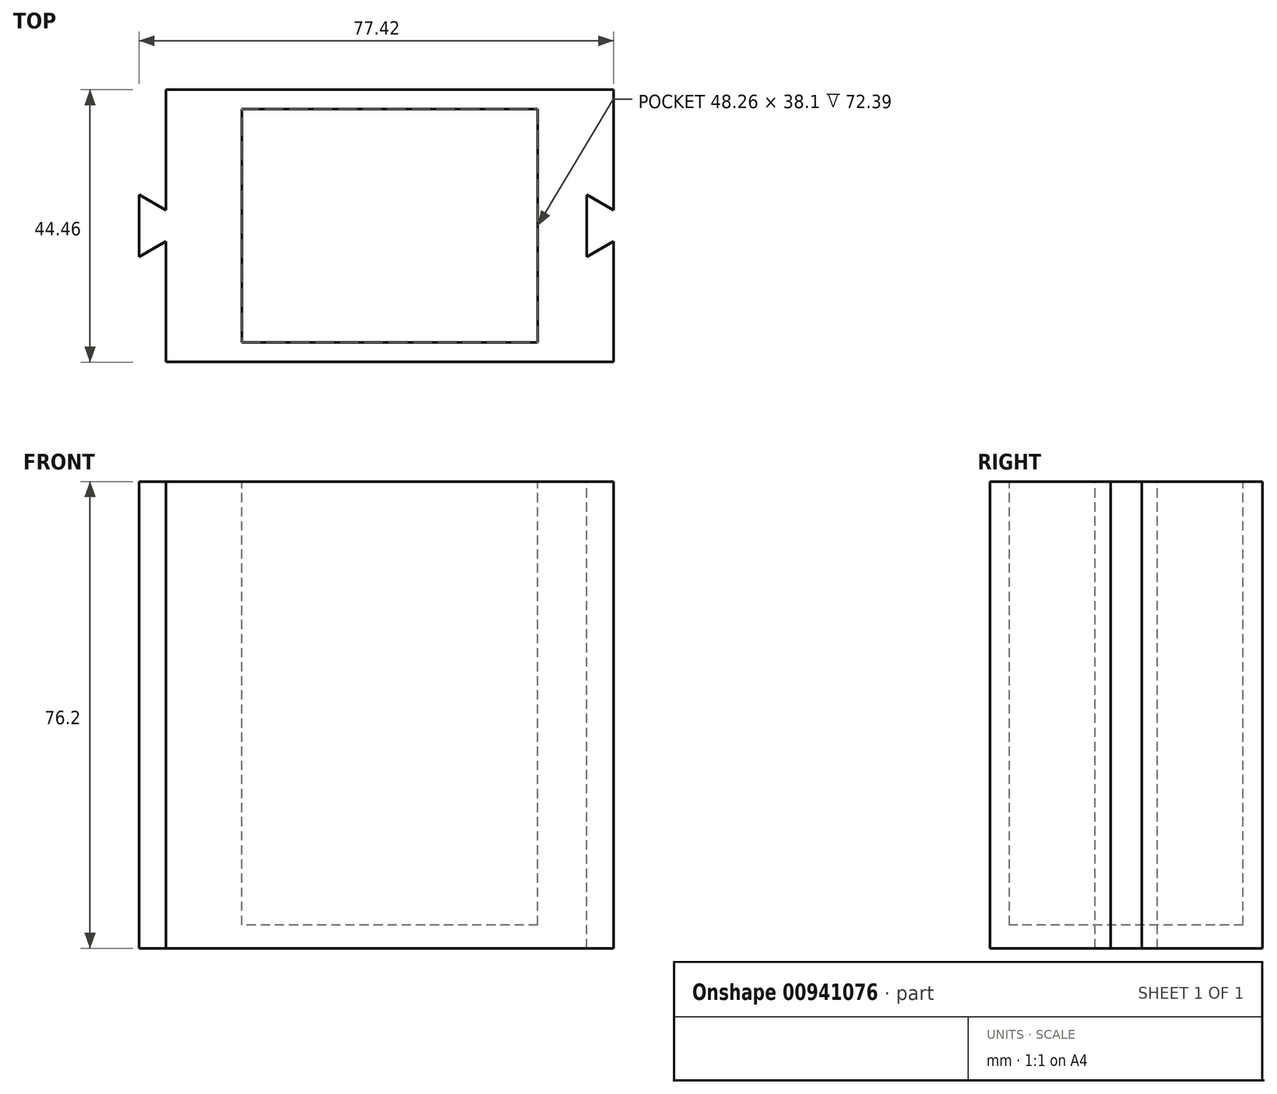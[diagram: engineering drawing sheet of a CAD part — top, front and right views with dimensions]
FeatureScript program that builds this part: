
annotation { "Feature Type Name" : "Feature", "Feature Type Description" : "" }
export const myFeature = defineFeature(function(context is Context, id is Id, definition is map)
    precondition{}
    {
        {
            var Q0;
            Q0=qCreatedBy(makeId("Top.planeOp"),FACE);
            var sketch = newSketch(context, id + "F0", { "sketchPlane" : qUnion([Q0])});
            skLineSegment(sketch, "E0.bottom", {"start": v(36.51, 22.23) * mm, "end": v(-36.51, 22.23) * mm});
            skLineSegment(sketch, "E0.top", {"start": v(36.51, -22.22) * mm, "end": v(-36.51, -22.22) * mm});
            skLineSegment(sketch, "E0.left", {"start": v(36.51, 22.23) * mm, "end": v(36.51, -22.22) * mm});
            skLineSegment(sketch, "E0.right", {"start": v(-36.51, 22.23) * mm, "end": v(-36.51, -22.22) * mm});
            skPoint(sketch, "E0.middle", {"position": v(0, 0) * mm});
            skSolve(sketch);
        }
        {
            var Q0;
            Q0=makeQuery(id+"F0.imprint","IMPRINT",FACE,{"disambiguationData":[TD([[makeQuery(id+"F0.imprint","IMPRINT",EDGE,{"derivedFrom":sQuery(id+"F0.wireOp",EDGE,"E0.bottom")}),1.0]])]});
            extrude(context, id + "F1", {"entities" : qUnion([Q0]), "depth" : 76.2 * mm, "offsetDistance" : 25.4 * mm});
        }
        {
            var Q0;
            Q0=makeQuery(id+"F1.opExtrude","CAP_FACE",FACE,{"disambiguationData":[OSD([sQuery(id+"F0.wireOp",EDGE,"E0.bottom"),sQuery(id+"F0.wireOp",EDGE,"E0.top"),sQuery(id+"F0.wireOp",EDGE,"E0.left"),sQuery(id+"F0.wireOp",EDGE,"E0.right")])],"isStart":false});
            var sketch = newSketch(context, id + "F2", { "sketchPlane" : qUnion([Q0])});
            skLineSegment(sketch, "E1.bottom", {"start": v(0, -22.22) * mm, "end": v(0, -22.22) * mm});
            skLineSegment(sketch, "E1.top", {"start": v(0, 66.68) * mm, "end": v(0, 66.68) * mm});
            skLineSegment(sketch, "E1.left", {"start": v(0, -22.22) * mm, "end": v(0, 66.68) * mm, "construction": true});
            skLineSegment(sketch, "E1.right", {"start": v(0, -22.22) * mm, "end": v(0, 66.68) * mm, "construction": true});
            skPoint(sketch, "E1.middle", {"position": v(0, 22.23) * mm});
            skLineSegment(sketch, "E2", {"start": v(-36.51, 0) * mm, "end": v(36.51, 0) * mm, "construction": true});
            skLineSegment(sketch, "E3.bottom", {"start": v(24.13, 19.05) * mm, "end": v(-24.13, 19.05) * mm});
            skLineSegment(sketch, "E3.top", {"start": v(24.13, -19.05) * mm, "end": v(-24.13, -19.05) * mm});
            skLineSegment(sketch, "E3.left", {"start": v(24.13, 19.05) * mm, "end": v(24.13, -19.05) * mm});
            skLineSegment(sketch, "E3.right", {"start": v(-24.13, 19.05) * mm, "end": v(-24.13, -19.05) * mm});
            skPoint(sketch, "E3.middle", {"position": v(0, 0) * mm});
            skSolve(sketch);
        }
        {
            var Q0;
            Q0=makeQuery(id+"F2.imprint","IMPRINT",FACE,{"disambiguationData":[TD([[makeQuery(id+"F2.imprint","IMPRINT",EDGE,{"derivedFrom":sQuery(id+"F2.wireOp",EDGE,"E3.bottom")}),1.0]])]});
            extrude(context, id + "F3", {"entities" : qUnion([Q0]), "operationType" : NewBodyOperationType.REMOVE, "oppositeDirection" : true, "depth" : 72.39 * mm, "offsetDistance" : 25.4 * mm});
        }
        {
            var Q0;
            Q0=makeQuery(id+"F1.opExtrude","CAP_FACE",FACE,{"disambiguationData":[OSD([sQuery(id+"F0.wireOp",EDGE,"E0.bottom"),sQuery(id+"F0.wireOp",EDGE,"E0.top"),sQuery(id+"F0.wireOp",EDGE,"E0.left"),sQuery(id+"F0.wireOp",EDGE,"E0.right")])],"isStart":false});
            var sketch = newSketch(context, id + "F4", { "sketchPlane" : qUnion([Q0])});
            skLineSegment(sketch, "E4", {"start": v(-36.51, 0) * mm, "end": v(36.51, 0) * mm, "construction": true});
            skLineSegment(sketch, "E5", {"start": v(36.51, 0) * mm, "end": v(36.51, -2.54) * mm});
            skLineSegment(sketch, "E6", {"start": v(36.51, -2.54) * mm, "end": v(32.11, -5.08) * mm});
            skLineSegment(sketch, "E7", {"start": v(32.11, -5.08) * mm, "end": v(32.11, 5.08) * mm});
            skLineSegment(sketch, "E8", {"start": v(32.11, 5.08) * mm, "end": v(36.51, 2.54) * mm});
            skLineSegment(sketch, "E9", {"start": v(36.51, 2.54) * mm, "end": v(36.51, -2.54) * mm});
            skLineSegment(sketch, "E10", {"start": v(36.51, 2.54) * mm, "end": v(36.51, 0) * mm});
            skLineSegment(sketch, "E11", {"start": v(-36.51, 2.54) * mm, "end": v(-40.91, 5.08) * mm});
            skLineSegment(sketch, "E12", {"start": v(-40.91, 5.08) * mm, "end": v(-40.91, -5.08) * mm});
            skLineSegment(sketch, "E13", {"start": v(-40.91, -5.08) * mm, "end": v(-36.51, -2.54) * mm});
            skLineSegment(sketch, "E14", {"start": v(-36.51, -2.54) * mm, "end": v(-36.51, 2.54) * mm});
            skLineSegment(sketch, "E15", {"start": v(-36.51, 2.54) * mm, "end": v(-36.51, 0) * mm});
            skSolve(sketch);
        }
        {
            var Q0;
            Q0=makeQuery(id+"F4.imprint","IMPRINT",FACE,{"disambiguationData":[TD([[makeQuery(id+"F4.imprint","IMPRINT",EDGE,{"derivedFrom":sQuery(id+"F4.wireOp",EDGE,"E6")}),-1.0]])]});
            extrude(context, id + "F5", {"entities" : qUnion([Q0]), "operationType" : NewBodyOperationType.REMOVE, "depth" : -76.2 * mm, "offsetDistance" : 25.4 * mm});
        }
        {
            var Q0;
            Q0=makeQuery(id+"F4.imprint","IMPRINT",FACE,{"disambiguationData":[TD([[makeQuery(id+"F4.imprint","IMPRINT",EDGE,{"derivedFrom":sQuery(id+"F4.wireOp",EDGE,"E11")}),1.0]])]});
            extrude(context, id + "F6", {"entities" : qUnion([Q0]), "operationType" : NewBodyOperationType.ADD, "depth" : -76.2 * mm, "offsetDistance" : 25.4 * mm});
        }
    });
